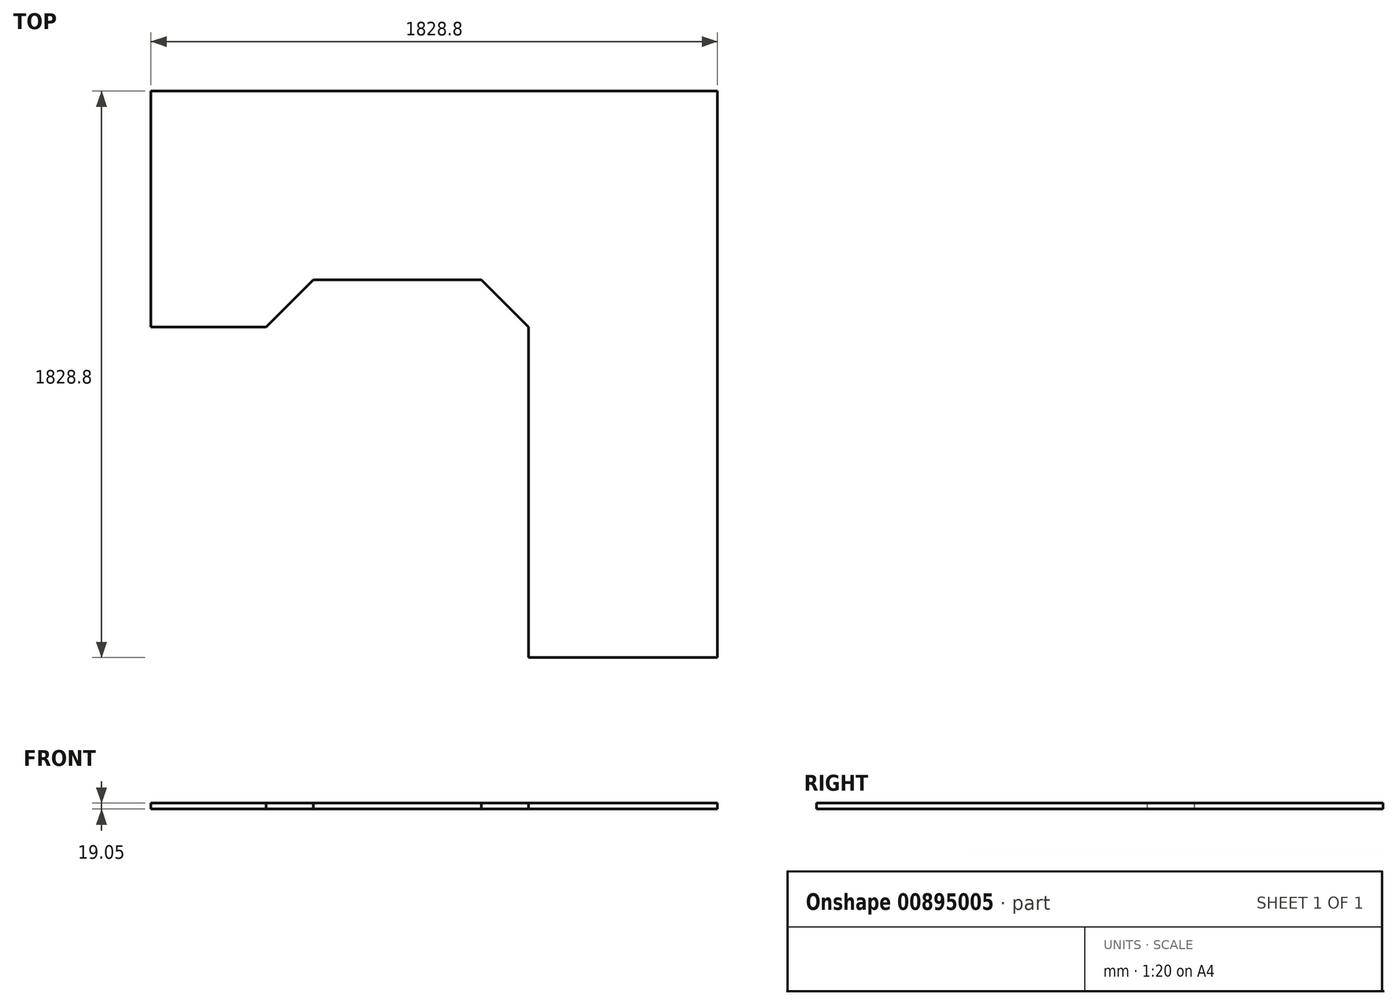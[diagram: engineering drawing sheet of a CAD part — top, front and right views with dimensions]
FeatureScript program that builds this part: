
annotation { "Feature Type Name" : "Feature", "Feature Type Description" : "" }
export const myFeature = defineFeature(function(context is Context, id is Id, definition is map)
    precondition{}
    {
        {
            var Q0;
            Q0=qCreatedBy(makeId("Top.planeOp"),FACE);
            var sketch = newSketch(context, id + "F0", { "sketchPlane" : qUnion([Q0])});
            skLineSegment(sketch, "E0.bottom", {"start": v(609.6, 609.6) * mm, "end": v(-1219.2, 609.6) * mm});
            skLineSegment(sketch, "E0.top", {"start": v(609.6, -1219.2) * mm, "end": v(0, -1219.2) * mm});
            skLineSegment(sketch, "E0.left", {"start": v(609.6, 609.6) * mm, "end": v(609.6, -1219.2) * mm});
            skLineSegment(sketch, "E0.right", {"start": v(-1219.2, 609.6) * mm, "end": v(-1219.2, -152.4) * mm});
            skLineSegment(sketch, "E1.top", {"start": v(-1219.2, -152.4) * mm, "end": v(-847.73, -152.4) * mm});
            skLineSegment(sketch, "E2", {"start": v(-847.73, -152.4) * mm, "end": v(-695.33, 0) * mm});
            skLineSegment(sketch, "E3", {"start": v(-695.33, 0) * mm, "end": v(-152.4, 0) * mm});
            skLineSegment(sketch, "E4", {"start": v(0, -152.4) * mm, "end": v(0, -1219.2) * mm});
            skLineSegment(sketch, "E5", {"start": v(-152.4, 0) * mm, "end": v(0, -152.4) * mm});
            skPoint(sketch, "E6.orphan", {"position": v(0, 0) * mm});
            skSolve(sketch);
        }
        {
            var Q0;
            Q0=makeQuery(id+"F0.imprint","IMPRINT",FACE,{"disambiguationData":[TD([[makeQuery(id+"F0.imprint","IMPRINT",EDGE,{"derivedFrom":sQuery(id+"F0.wireOp",EDGE,"E0.bottom")}),1.0]])]});
            extrude(context, id + "F1", {"entities" : qUnion([Q0]), "depth" : 19.05 * mm, "offsetDistance" : 25.4 * mm});
        }
    });
